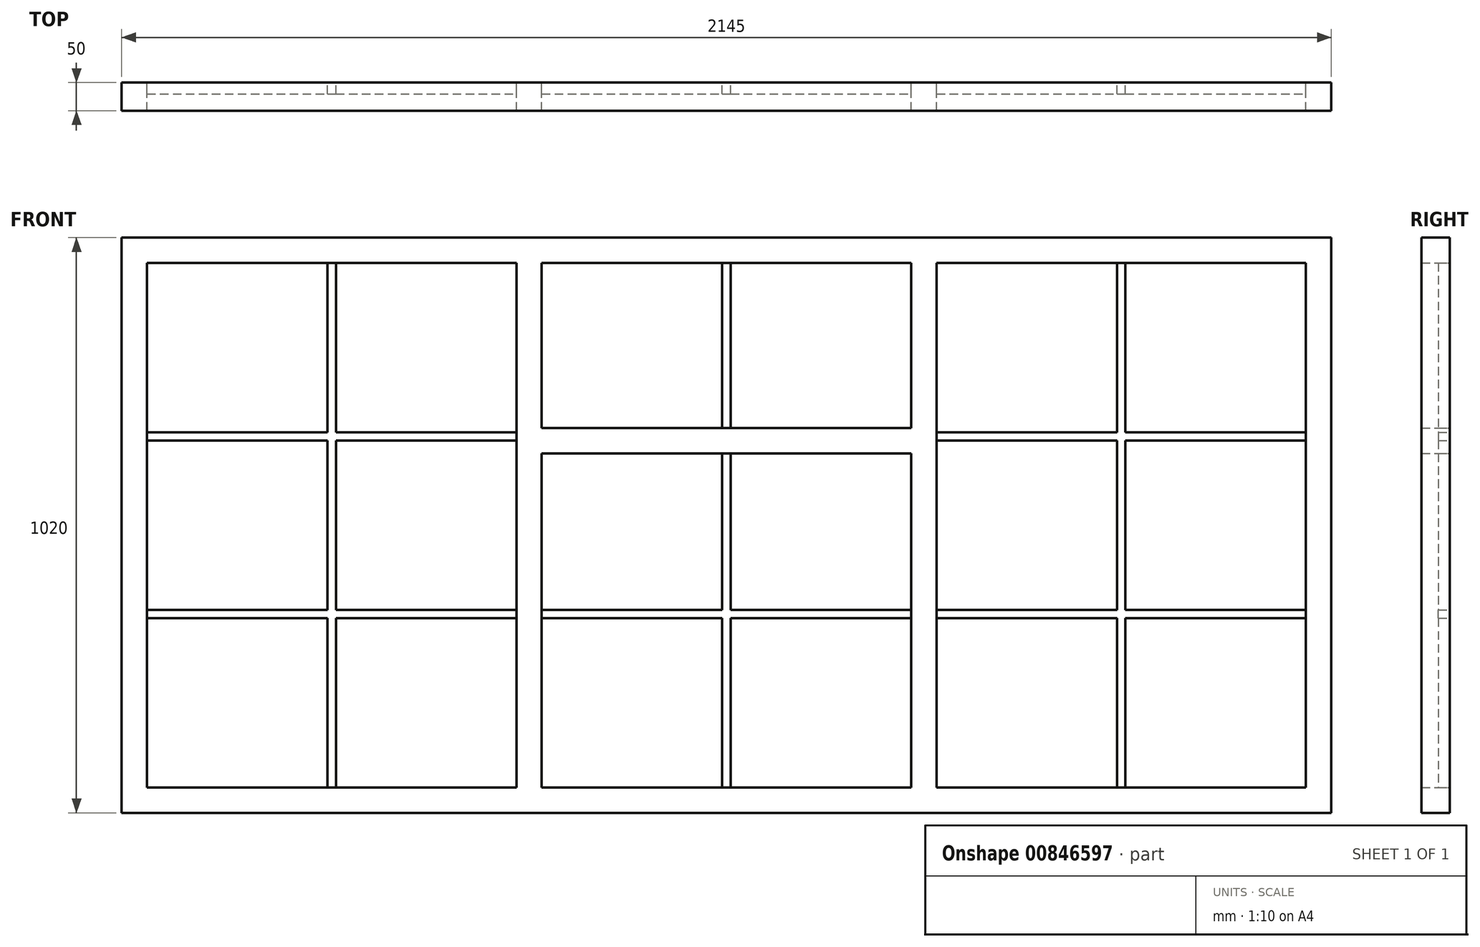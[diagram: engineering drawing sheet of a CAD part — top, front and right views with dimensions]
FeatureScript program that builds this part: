
annotation { "Feature Type Name" : "Feature", "Feature Type Description" : "" }
export const myFeature = defineFeature(function(context is Context, id is Id, definition is map)
    precondition{}
    {
        {
            var Q0;
            Q0=qCreatedBy(makeId("Front.planeOp"),FACE);
            var sketch = newSketch(context, id + "F0", { "sketchPlane" : qUnion([Q0])});
            skLineSegment(sketch, "E0.bottom", {"start": v(0, 0) * mm, "end": v(2145, 0) * mm});
            skLineSegment(sketch, "E0.top", {"start": v(0, 1020) * mm, "end": v(2145, 1020) * mm});
            skLineSegment(sketch, "E0.left", {"start": v(0, 0) * mm, "end": v(0, 1020) * mm});
            skLineSegment(sketch, "E0.right", {"start": v(2145, 0) * mm, "end": v(2145, 1020) * mm});
            skLineSegment(sketch, "E1.bottom", {"start": v(45, 975) * mm, "end": v(700, 975) * mm});
            skLineSegment(sketch, "E1.top", {"start": v(45, 45) * mm, "end": v(700, 45) * mm});
            skLineSegment(sketch, "E1.left", {"start": v(45, 975) * mm, "end": v(45, 45) * mm});
            skLineSegment(sketch, "E1.right", {"start": v(700, 975) * mm, "end": v(700, 45) * mm});
            skLineSegment(sketch, "E2.bottom", {"start": v(745, 975) * mm, "end": v(1400, 975) * mm});
            skLineSegment(sketch, "E2.top", {"start": v(745, 682.5) * mm, "end": v(1400, 682.5) * mm});
            skLineSegment(sketch, "E2.left", {"start": v(745, 975) * mm, "end": v(745, 682.5) * mm});
            skLineSegment(sketch, "E2.right", {"start": v(1400, 975) * mm, "end": v(1400, 682.5) * mm});
            skLineSegment(sketch, "E3.bottom", {"start": v(745, 637.5) * mm, "end": v(1400, 637.5) * mm});
            skLineSegment(sketch, "E3.top", {"start": v(745, 45) * mm, "end": v(1400, 45) * mm});
            skLineSegment(sketch, "E3.left", {"start": v(745, 637.5) * mm, "end": v(745, 45) * mm});
            skLineSegment(sketch, "E3.right", {"start": v(1400, 637.5) * mm, "end": v(1400, 45) * mm});
            skLineSegment(sketch, "E4.bottom", {"start": v(1445, 975) * mm, "end": v(2100, 975) * mm});
            skLineSegment(sketch, "E4.top", {"start": v(1445, 45) * mm, "end": v(2100, 45) * mm});
            skLineSegment(sketch, "E4.left", {"start": v(1445, 975) * mm, "end": v(1445, 45) * mm});
            skLineSegment(sketch, "E4.right", {"start": v(2100, 975) * mm, "end": v(2100, 45) * mm});
            skSolve(sketch);
        }
        {
            var Q0;
            Q0=qSketchRegion(id+"F0",true);
            extrude(context, id + "F1", {"entities" : qUnion([Q0]), "depth" : 50 * mm, "offsetDistance" : 25 * mm});
        }
        {
            var Q0;
            Q0=qCreatedBy(makeId("Front.planeOp"),FACE);
            var sketch = newSketch(context, id + "F2", { "sketchPlane" : qUnion([Q0])});
            skLineSegment(sketch, "E5.bottom", {"start": v(1765, 975) * mm, "end": v(1780, 975) * mm});
            skLineSegment(sketch, "E5.top", {"start": v(1765, 45) * mm, "end": v(1780, 45) * mm});
            skLineSegment(sketch, "E5.left", {"start": v(1765, 975) * mm, "end": v(1765, 660) * mm});
            skLineSegment(sketch, "E5.right", {"start": v(1780, 975) * mm, "end": v(1780, 660) * mm});
            skLineSegment(sketch, "E6.bottom", {"start": v(1445, 660) * mm, "end": v(1765, 660) * mm});
            skLineSegment(sketch, "E6.top", {"start": v(1445, 675) * mm, "end": v(1765, 675) * mm});
            skLineSegment(sketch, "E6.left", {"start": v(1445, 675) * mm, "end": v(1445, 660) * mm});
            skLineSegment(sketch, "E6.right", {"start": v(2100, 675) * mm, "end": v(2100, 660) * mm});
            skLineSegment(sketch, "E7.bottom", {"start": v(1445, 345) * mm, "end": v(1765, 345) * mm});
            skLineSegment(sketch, "E7.top", {"start": v(1445, 360) * mm, "end": v(1765, 360) * mm});
            skLineSegment(sketch, "E7.left", {"start": v(1445, 345) * mm, "end": v(1445, 360) * mm});
            skLineSegment(sketch, "E7.right", {"start": v(2100, 345) * mm, "end": v(2100, 360) * mm});
            skLineSegment(sketch, "E8.trimOffspring", {"start": v(1765, 675) * mm, "end": v(1765, 360) * mm});
            skLineSegment(sketch, "E9.trimOffspring", {"start": v(1780, 660) * mm, "end": v(2100, 660) * mm});
            skLineSegment(sketch, "E10.trimOffspring", {"start": v(1780, 675) * mm, "end": v(1780, 360) * mm});
            skLineSegment(sketch, "E11.trimOffspring", {"start": v(1780, 675) * mm, "end": v(2100, 675) * mm});
            skLineSegment(sketch, "E12.trimOffspring", {"start": v(1780, 360) * mm, "end": v(2100, 360) * mm});
            skLineSegment(sketch, "E13.trimOffspring", {"start": v(1765, 345) * mm, "end": v(1765, 45) * mm});
            skLineSegment(sketch, "E14.trimOffspring", {"start": v(1780, 345) * mm, "end": v(2100, 345) * mm});
            skLineSegment(sketch, "E15.trimOffspring", {"start": v(1780, 345) * mm, "end": v(1780, 45) * mm});
            skLineSegment(sketch, "E16.bottom", {"start": v(1065, 975) * mm, "end": v(1080, 975) * mm});
            skLineSegment(sketch, "E16.top", {"start": v(1065, 682.5) * mm, "end": v(1080, 682.5) * mm});
            skLineSegment(sketch, "E16.left", {"start": v(1065, 975) * mm, "end": v(1065, 682.5) * mm});
            skLineSegment(sketch, "E16.right", {"start": v(1080, 975) * mm, "end": v(1080, 682.5) * mm});
            skLineSegment(sketch, "E17.bottom", {"start": v(1065, 637.5) * mm, "end": v(1080, 637.5) * mm});
            skLineSegment(sketch, "E17.top", {"start": v(1065, 45) * mm, "end": v(1080, 45) * mm});
            skLineSegment(sketch, "E17.left", {"start": v(1065, 637.5) * mm, "end": v(1065, 360) * mm});
            skLineSegment(sketch, "E17.right", {"start": v(1080, 637.5) * mm, "end": v(1080, 360) * mm});
            skLineSegment(sketch, "E18.bottom", {"start": v(745, 360) * mm, "end": v(1065, 360) * mm});
            skLineSegment(sketch, "E18.top", {"start": v(745, 345) * mm, "end": v(1065, 345) * mm});
            skLineSegment(sketch, "E18.left", {"start": v(745, 360) * mm, "end": v(745, 345) * mm});
            skLineSegment(sketch, "E18.right", {"start": v(1400, 360) * mm, "end": v(1400, 345) * mm});
            skLineSegment(sketch, "E19.trimOffspring", {"start": v(1080, 360) * mm, "end": v(1400, 360) * mm});
            skLineSegment(sketch, "E20.trimOffspring", {"start": v(1065, 345) * mm, "end": v(1065, 45) * mm});
            skLineSegment(sketch, "E21.trimOffspring", {"start": v(1080, 345) * mm, "end": v(1400, 345) * mm});
            skLineSegment(sketch, "E22.trimOffspring", {"start": v(1080, 345) * mm, "end": v(1080, 45) * mm});
            skLineSegment(sketch, "E23.bottom", {"start": v(365, 975) * mm, "end": v(380, 975) * mm});
            skLineSegment(sketch, "E23.top", {"start": v(365, 45) * mm, "end": v(380, 45) * mm});
            skLineSegment(sketch, "E23.left", {"start": v(365, 975) * mm, "end": v(365, 675) * mm});
            skLineSegment(sketch, "E23.right", {"start": v(380, 975) * mm, "end": v(380, 675) * mm});
            skLineSegment(sketch, "E24.bottom", {"start": v(45, 660) * mm, "end": v(365, 660) * mm});
            skLineSegment(sketch, "E24.top", {"start": v(45, 675) * mm, "end": v(365, 675) * mm});
            skLineSegment(sketch, "E24.left", {"start": v(45, 675) * mm, "end": v(45, 660) * mm});
            skLineSegment(sketch, "E24.right", {"start": v(700, 675) * mm, "end": v(700, 660) * mm});
            skLineSegment(sketch, "E25.bottom", {"start": v(45, 360) * mm, "end": v(365, 360) * mm});
            skLineSegment(sketch, "E25.top", {"start": v(45, 345) * mm, "end": v(365, 345) * mm});
            skLineSegment(sketch, "E25.left", {"start": v(45, 360) * mm, "end": v(45, 345) * mm});
            skLineSegment(sketch, "E25.right", {"start": v(700, 360) * mm, "end": v(700, 345) * mm});
            skLineSegment(sketch, "E26.trimOffspring", {"start": v(380, 675) * mm, "end": v(700, 675) * mm});
            skLineSegment(sketch, "E27.trimOffspring", {"start": v(365, 660) * mm, "end": v(365, 360) * mm});
            skLineSegment(sketch, "E28.trimOffspring", {"start": v(380, 660) * mm, "end": v(700, 660) * mm});
            skLineSegment(sketch, "E29.trimOffspring", {"start": v(380, 660) * mm, "end": v(380, 360) * mm});
            skLineSegment(sketch, "E30.trimOffspring", {"start": v(380, 360) * mm, "end": v(700, 360) * mm});
            skLineSegment(sketch, "E31.trimOffspring", {"start": v(365, 345) * mm, "end": v(365, 45) * mm});
            skLineSegment(sketch, "E32.trimOffspring", {"start": v(380, 345) * mm, "end": v(700, 345) * mm});
            skLineSegment(sketch, "E33.trimOffspring", {"start": v(380, 345) * mm, "end": v(380, 45) * mm});
            skSolve(sketch);
        }
        {
            var Q0;
            Q0 = qSketchRegion(id + "F2", true);
            extrude(context, id + "F3", {"entities" : qUnion([Q0]), "operationType" : NewBodyOperationType.ADD, "depth" : 20 * mm, "offsetDistance" : 25 * mm});
        }
    });
